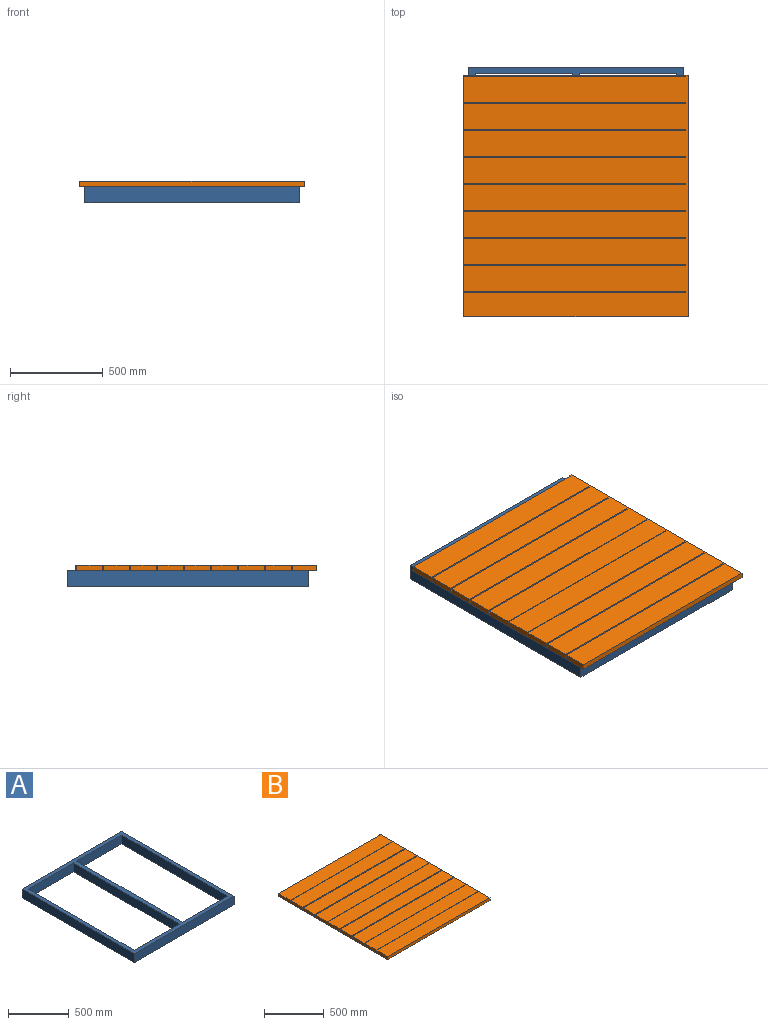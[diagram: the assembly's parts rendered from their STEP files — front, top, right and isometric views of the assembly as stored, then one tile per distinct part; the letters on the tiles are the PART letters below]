
ASSEMBLY  parts=2 mates=1
PART A: 28 faces, bbox 1162.7x1304.9x88.9 mm
  f0: plane 1231.9x88.9mm, normal (1,0,0), area 109515.8mm2, adj f6,f8,f14,f15,f24,f25,f26,f27
  f1: plane 1231.9x88.9mm, normal (-1,0,0), area 109515.8mm2, adj f6,f8,f14,f15,f24,f25,f26,f27
  f2: plane 1162.69x88.9mm, normal (0,-1,0), area 103362.9mm2, adj f3,f4,f7,f9,f10,f11,f12,f15
  f3: plane 1304.93x36.51mm, normal (0,0,-1), area 47646.1mm2, adj f2,f9,f11,f13
  f4: plane 1089.61x36.51mm, normal (0,0,-1), area 39784.5mm2, adj f2,f8,f21,f23
  f5: plane 1089.61x36.51mm, normal (0,0,-1), area 39784.5mm2, adj f13,f14,f17,f19
  f6: plane 1231.85x36.51mm, normal (0,0,-1), area 44977.9mm2, adj f0,f1,f24,f26
  f7: plane 1304.93x36.51mm, normal (0,0,-1), area 47646.1mm2, adj f2,f10,f12,f13
  f8: plane 1089.66x88.9mm, normal (0,1,0), area 93717.8mm2, adj f0,f1,f4,f9,f10,f15,f20,f21
  f9: plane 1304.93x88.9mm, normal (-1,0,0), area 109701.4mm2, adj f2,f3,f8,f13,f14,f15,f16,f22
  f10: plane 1304.93x88.9mm, normal (1,0,0), area 109701.4mm2, adj f2,f7,f8,f13,f14,f15,f18,f20
  f11: plane 1304.93x88.9mm, normal (1,0,0), area 116007.8mm2, adj f2,f3,f13,f15
  f12: plane 1304.93x88.9mm, normal (-1,0,0), area 116007.8mm2, adj f2,f7,f13,f15
  f13: plane 1162.69x88.9mm, normal (0,1,0), area 103362.9mm2, adj f3,f5,f7,f9,f10,f11,f12,f15
  f14: plane 1089.66x88.9mm, normal (0,-1,0), area 93717.8mm2, adj f0,f1,f5,f9,f10,f15,f16,f17
  f15: plane 1304.93x1162.69mm, normal (0,0,1), area 219844.6mm2, adj f0,f1,f2,f8,f9,f10,f11,f12
  f16: plane 36.51x0.03mm, normal (0,0,-1), area 0.9mm2, adj f9,f13,f14,f17
  f17: plane 36.51x2.54mm, normal (1,0,0), area 92.7mm2, adj f5,f13,f14,f16
  f18: plane 36.51x0.03mm, normal (0,0,-1), area 0.9mm2, adj f10,f13,f14,f19
  f19: plane 36.51x2.54mm, normal (-1,0,0), area 92.7mm2, adj f5,f13,f14,f18
  f20: plane 36.51x0.03mm, normal (0,0,-1), area 0.9mm2, adj f2,f8,f10,f21
  f21: plane 36.51x2.54mm, normal (-1,0,0), area 92.7mm2, adj f2,f4,f8,f20
  f22: plane 36.51x0.03mm, normal (0,0,-1), area 0.9mm2, adj f2,f8,f9,f23
  f23: plane 36.51x2.54mm, normal (1,0,0), area 92.7mm2, adj f2,f4,f8,f22
  f24: plane 36.51x2.54mm, normal (0,-1,0), area 92.7mm2, adj f0,f1,f6,f25
  f25: plane 36.51x0.03mm, normal (0,0,-1), area 0.9mm2, adj f0,f1,f8,f24
  f26: plane 36.51x2.54mm, normal (0,1,0), area 92.7mm2, adj f0,f1,f6,f27
  f27: plane 36.51x0.03mm, normal (0,0,-1), area 0.9mm2, adj f0,f1,f14,f26
PART B: 41 faces, bbox 1213.5x1304.9x29.4 mm
  f0: plane 1213.49x29.37mm, normal (0,1,0), area 8951.1mm2, adj f1,f2,f4,f5,f39,f40
  f1: plane 1304.93x29.37mm, normal (-1,0,0), area 37053.9mm2, adj f0,f2,f3,f5,f6,f8,f9,f10
  f2: plane 1304.93x1213.49mm, normal (0,0,1), area 1514887.1mm2, adj f0,f1,f3,f4,f6,f7,f8,f10
  f3: plane 1213.49x29.37mm, normal (0,-1,0), area 35638.7mm2, adj f1,f2,f4,f5
  f4: plane 1304.93x29.37mm, normal (1,0,0), area 38324mm2, adj f0,f2,f3,f5
  f5: plane 1304.93x1213.49mm, normal (0,0,-1), area 1583512.2mm2, adj f0,f1,f3,f4
  f6: plane 1200.79x22.23mm, normal (0,1,0), area 26687.5mm2, adj f1,f2,f7,f9
  f7: plane 22.23x6.35mm, normal (-1,0,0), area 141.1mm2, adj f2,f6,f8,f9
  f8: plane 1200.79x22.23mm, normal (0,-1,0), area 26687.5mm2, adj f1,f2,f7,f9
  f9: plane 1200.79x6.35mm, normal (0,0,1), area 7625mm2, adj f1,f6,f7,f8
  f10: plane 1200.79x22.23mm, normal (0,1,0), area 26687.5mm2, adj f1,f2,f11,f13
  f11: plane 22.23x6.35mm, normal (-1,0,0), area 141.1mm2, adj f2,f10,f12,f13
  f12: plane 1200.79x22.23mm, normal (0,-1,0), area 26687.5mm2, adj f1,f2,f11,f13
  f13: plane 1200.79x6.35mm, normal (0,0,1), area 7625mm2, adj f1,f10,f11,f12
  f14: plane 1200.79x22.23mm, normal (0,1,0), area 26687.5mm2, adj f1,f2,f15,f17
  f15: plane 22.23x6.35mm, normal (-1,0,0), area 141.1mm2, adj f2,f14,f16,f17
  f16: plane 1200.79x22.23mm, normal (0,-1,0), area 26687.5mm2, adj f1,f2,f15,f17
  f17: plane 1200.79x6.35mm, normal (0,0,1), area 7625mm2, adj f1,f14,f15,f16
  f18: plane 1200.79x22.23mm, normal (0,1,0), area 26687.5mm2, adj f1,f2,f19,f21
  f19: plane 22.23x6.35mm, normal (-1,0,0), area 141.1mm2, adj f2,f18,f20,f21
  f20: plane 1200.79x22.23mm, normal (0,-1,0), area 26687.5mm2, adj f1,f2,f19,f21
  f21: plane 1200.79x6.35mm, normal (0,0,1), area 7625mm2, adj f1,f18,f19,f20
  f22: plane 1200.79x22.23mm, normal (0,1,0), area 26687.5mm2, adj f1,f2,f23,f25
  f23: plane 22.23x6.35mm, normal (-1,0,0), area 141.1mm2, adj f2,f22,f24,f25
  f24: plane 1200.79x22.23mm, normal (0,-1,0), area 26687.5mm2, adj f1,f2,f23,f25
  f25: plane 1200.79x6.35mm, normal (0,0,1), area 7625mm2, adj f1,f22,f23,f24
  f26: plane 1200.79x22.23mm, normal (0,1,0), area 26687.5mm2, adj f1,f2,f27,f29
  f27: plane 22.23x6.35mm, normal (-1,0,0), area 141.1mm2, adj f2,f26,f28,f29
  f28: plane 1200.79x22.23mm, normal (0,-1,0), area 26687.5mm2, adj f1,f2,f27,f29
  f29: plane 1200.79x6.35mm, normal (0,0,1), area 7625mm2, adj f1,f26,f27,f28
  f30: plane 1200.79x22.23mm, normal (0,1,0), area 26687.5mm2, adj f1,f2,f31,f33
  f31: plane 22.23x6.35mm, normal (-1,0,0), area 141.1mm2, adj f2,f30,f32,f33
  f32: plane 1200.79x22.23mm, normal (0,-1,0), area 26687.5mm2, adj f1,f2,f31,f33
  f33: plane 1200.79x6.35mm, normal (0,0,1), area 7625mm2, adj f1,f30,f31,f32
  f34: plane 1200.79x22.23mm, normal (0,1,0), area 26687.5mm2, adj f1,f2,f35,f37
  f35: plane 22.23x6.35mm, normal (-1,0,0), area 141.1mm2, adj f2,f34,f36,f37
  f36: plane 1200.79x22.23mm, normal (0,-1,0), area 26687.5mm2, adj f1,f2,f35,f37
  f37: plane 1200.79x6.35mm, normal (0,0,1), area 7625mm2, adj f1,f34,f35,f36
  f38: plane 1200.79x22.23mm, normal (0,1,0), area 26687.5mm2, adj f1,f2,f39,f40
  f39: plane 22.23x6.35mm, normal (-1,0,0), area 141.1mm2, adj f0,f2,f38,f40
  f40: plane 1200.79x6.35mm, normal (0,0,1), area 7625mm2, adj f0,f1,f38,f39
PLACE A t=(3556,3198.81,0)mm
PLACE B t=(12.7,608.01,88.9)mm
MATE fastened A.f15 <-> B.f5  axis (0,0,1) through (-581.34,0,88.9)mm
